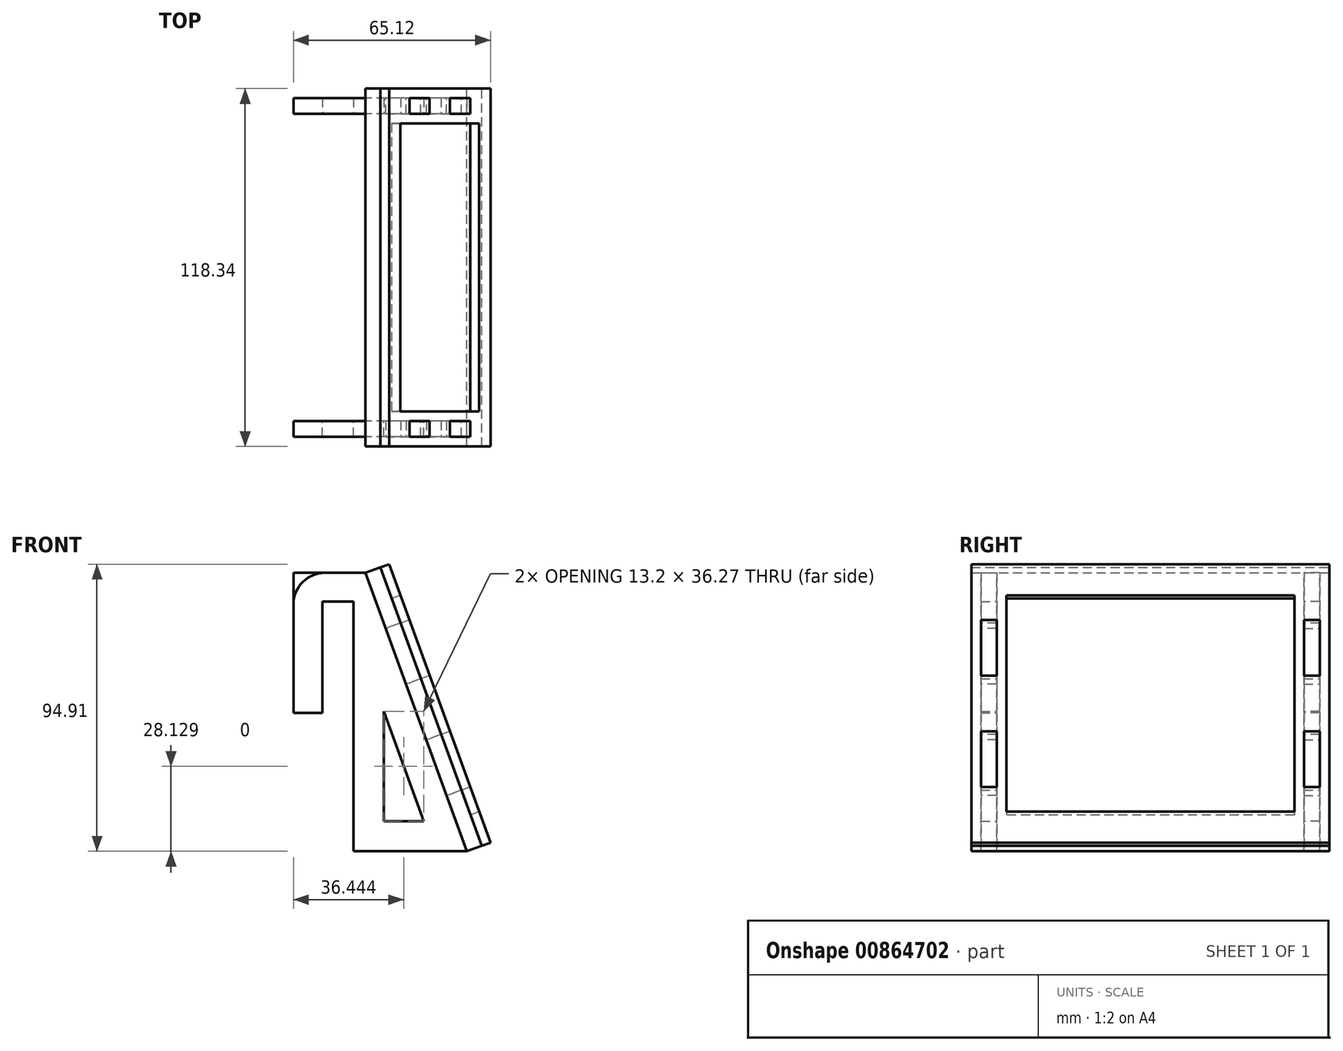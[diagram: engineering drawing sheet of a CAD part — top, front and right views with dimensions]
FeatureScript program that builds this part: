
annotation { "Feature Type Name" : "Feature", "Feature Type Description" : "" }
export const myFeature = defineFeature(function(context is Context, id is Id, definition is map)
    precondition{}
    {
        {
            assignVariable(context, id + "F0", {"name" : "thickness", "anyValue" : 5.2});
        }
        {
            var Q0;
            Q0=qCreatedBy(makeId("Front.planeOp"),FACE);
            cPlane(context, id + "F1", {"entities" : qUnion([Q0]), "cplaneType" : CPlaneType.OFFSET, "offset" : 50.8 * mm, "width" : 150 * mm, "height" : 150 * mm});
        }
        {
            var Q0;
            Q0=qCreatedBy(id+"F1.planeOp",FACE);
            var sketch = newSketch(context, id + "F2", { "sketchPlane" : qUnion([Q0])});
            skLineSegment(sketch, "E0", {"start": v(9.52, 0) * mm, "end": v(9.52, 36.73) * mm});
            skLineSegment(sketch, "E1", {"start": v(9.52, 36.73) * mm, "end": v(19.84, 36.73) * mm});
            skLineSegment(sketch, "E2", {"start": v(19.84, 36.73) * mm, "end": v(19.84, -45.82) * mm});
            skLineSegment(sketch, "E3", {"start": v(19.84, -45.82) * mm, "end": v(57.33, -45.82) * mm});
            skLineSegment(sketch, "E4", {"start": v(57.33, -45.82) * mm, "end": v(23.81, 46.25) * mm});
            skLineSegment(sketch, "E5", {"start": v(23.81, 46.25) * mm, "end": v(0, 46.25) * mm});
            skLineSegment(sketch, "E6", {"start": v(0, 46.25) * mm, "end": v(0, 0) * mm});
            skLineSegment(sketch, "E7", {"start": v(0, 0) * mm, "end": v(9.52, 0) * mm});
            skLineSegment(sketch, "E8", {"start": v(14.68, 36.73) * mm, "end": v(14.68, 46.25) * mm, "construction": true});
            skLineSegment(sketch, "E9", {"start": v(19.84, 36.73) * mm, "end": v(19.84, 46.25) * mm, "construction": true});
            skLineSegment(sketch, "E10.0", {"start": v(43.04, -35.82) * mm, "end": v(29.84, 0.44) * mm});
            skLineSegment(sketch, "E10.1", {"start": v(29.84, -35.82) * mm, "end": v(43.04, -35.82) * mm});
            skLineSegment(sketch, "E10.2", {"start": v(29.84, 0.44) * mm, "end": v(29.84, -35.82) * mm});
            skSolve(sketch);
        }
        {
            var Q0;
            Q0=makeQuery(id+"F2.imprint","IMPRINT",FACE,{"disambiguationData":[TD([[makeQuery(id+"F2.imprint","IMPRINT",EDGE,{"derivedFrom":sQuery(id+"F2.wireOp",EDGE,"E0")}),1.0]])]});
            extrude(context, id + "F3", {"entities" : qUnion([Q0]), "depth" : (getVariable(context, 'thickness')) * mm, "offsetDistance" : 25 * mm});
        }
        {
            var Q0;
            Q0=makeQuery(id+"F3.opExtrude","SWEPT_FACE",FACE,{"disambiguationData":[OSD([sQuery(id+"F2.wireOp",EDGE,"E4")])]});
            var sketch = newSketch(context, id + "F4", { "sketchPlane" : qUnion([Q0])});
            skLineSegment(sketch, "E11.0.0", {"start": v(-50.8, -62.67) * mm, "end": v(-50.8, 35.32) * mm});
            skLineSegment(sketch, "E11.0.1", {"start": v(-50.8, 35.32) * mm, "end": v(-56, 35.32) * mm});
            skLineSegment(sketch, "E11.0.2", {"start": v(-56, 35.32) * mm, "end": v(-56, -62.67) * mm});
            skLineSegment(sketch, "E11.0.3", {"start": v(-56, -62.67) * mm, "end": v(-50.8, -62.67) * mm});
            skLineSegment(sketch, "E12.bottom", {"start": v(-50.8, 15.72) * mm, "end": v(-56, 15.72) * mm});
            skLineSegment(sketch, "E12.top", {"start": v(-50.8, -3.88) * mm, "end": v(-56, -3.88) * mm});
            skLineSegment(sketch, "E12.left", {"start": v(-50.8, 15.72) * mm, "end": v(-50.8, -3.88) * mm});
            skLineSegment(sketch, "E12.right", {"start": v(-56, 15.72) * mm, "end": v(-56, -3.88) * mm});
            skLineSegment(sketch, "E13.bottom", {"start": v(-50.8, -23.47) * mm, "end": v(-56, -23.47) * mm});
            skLineSegment(sketch, "E13.top", {"start": v(-50.8, -43.07) * mm, "end": v(-56, -43.07) * mm});
            skLineSegment(sketch, "E13.left", {"start": v(-50.8, -23.47) * mm, "end": v(-50.8, -43.07) * mm});
            skLineSegment(sketch, "E13.right", {"start": v(-56, -23.47) * mm, "end": v(-56, -43.07) * mm});
            skLineSegment(sketch, "E14", {"start": v(-53.4, 35.32) * mm, "end": v(-53.4, 15.72) * mm, "construction": true});
            skLineSegment(sketch, "E15", {"start": v(-53.4, -43.07) * mm, "end": v(-53.4, -62.67) * mm, "construction": true});
            skLineSegment(sketch, "E16", {"start": v(-53.4, 15.72) * mm, "end": v(-53.4, -3.88) * mm, "construction": true});
            skLineSegment(sketch, "E17", {"start": v(-53.4, -3.88) * mm, "end": v(-53.4, -23.47) * mm, "construction": true});
            skLineSegment(sketch, "E18", {"start": v(-53.4, -23.47) * mm, "end": v(-53.4, -43.07) * mm, "construction": true});
            skSolve(sketch);
        }
        {
            var Q0;
            Q0=makeQuery(id+"F4.imprint","IMPRINT",FACE,{"disambiguationData":[TD([[makeQuery(id+"F4.imprint","IMPRINT",EDGE,{"derivedFrom":sQuery(id+"F4.wireOp",EDGE,"E12.bottom")}),1.0]])]});
            var Q1;
            Q1=makeQuery(id+"F4.imprint","IMPRINT",FACE,{"disambiguationData":[TD([[makeQuery(id+"F4.imprint","IMPRINT",EDGE,{"derivedFrom":sQuery(id+"F4.wireOp",EDGE,"E13.bottom")}),1.0]])]});
            extrude(context, id + "F5", {"entities" : qUnion([Q0, Q1]), "operationType" : NewBodyOperationType.ADD, "depth" : (getVariable(context, 'thickness') + 3.1) * mm, "offsetDistance" : 25 * mm});
        }
        {
            var Q0;
            Q0=makeQuery(id+"F3.opExtrude","SWEPT_BODY",BODY,{"disambiguationData":[OSD([sQuery(id+"F2.wireOp",EDGE,"E0"),sQuery(id+"F2.wireOp",EDGE,"E1"),sQuery(id+"F2.wireOp",EDGE,"E2"),sQuery(id+"F2.wireOp",EDGE,"E3"),sQuery(id+"F2.wireOp",EDGE,"E4"),sQuery(id+"F2.wireOp",EDGE,"E5"),sQuery(id+"F2.wireOp",EDGE,"E6"),sQuery(id+"F2.wireOp",EDGE,"E7"),sQuery(id+"F2.wireOp",EDGE,"013d1d72-8f7b-4af2-89c1-0a6e57d8ea99.0"),sQuery(id+"F2.wireOp",EDGE,"013d1d72-8f7b-4af2-89c1-0a6e57d8ea99.1"),sQuery(id+"F2.wireOp",EDGE,"013d1d72-8f7b-4af2-89c1-0a6e57d8ea99.2")])]});
            var Q1;
            Q1=qCreatedBy(makeId("Front.planeOp"),FACE);
            mirror(context, id + "F6", {"entities" : qUnion([Q0]), "mirrorPlane" : qUnion([Q1])});
        }
        {
            var Q0;
            {var subQ5=sQuery(id+"F2.wireOp",EDGE,"E5");var subQ6=sQuery(id+"F2.wireOp",EDGE,"E4");Q0=makeQuery(id+"F5.boolean.opBoolean","SPLIT",FACE,{"disambiguationData":[TD([makeQuery(id+"F3.opExtrude","SWEPT_FACE",FACE,{"disambiguationData":[OSD([subQ5])]})])],"derivedFrom":makeQuery(id+"F3.opExtrude","SWEPT_FACE",FACE,{"disambiguationData":[OSD([subQ6])]})});}
            var sketch = newSketch(context, id + "F7", { "sketchPlane" : qUnion([Q0])});
            skLineSegment(sketch, "E19.bottom", {"start": v(-59.18, 35.32) * mm, "end": v(59.18, 35.32) * mm});
            skLineSegment(sketch, "E19.top", {"start": v(-59.18, -62.67) * mm, "end": v(59.18, -62.67) * mm});
            skLineSegment(sketch, "E19.left", {"start": v(-59.18, 35.32) * mm, "end": v(-59.18, -62.67) * mm});
            skLineSegment(sketch, "E19.right", {"start": v(59.18, 35.32) * mm, "end": v(59.18, -62.67) * mm});
            skPoint(sketch, "E20.0", {"position": v(-56, 25.52) * mm});
            skLineSegment(sketch, "E21.0.0", {"start": v(-56, 15.72) * mm, "end": v(-50.8, 15.72) * mm, "construction": true});
            skLineSegment(sketch, "E21.0.1", {"start": v(-50.8, 15.72) * mm, "end": v(-50.8, 35.32) * mm, "construction": true});
            skLineSegment(sketch, "E21.0.2", {"start": v(-50.8, 35.32) * mm, "end": v(-56, 35.32) * mm, "construction": true});
            skLineSegment(sketch, "E21.0.3", {"start": v(-56, 35.32) * mm, "end": v(-56, 15.72) * mm, "construction": true});
            skLineSegment(sketch, "E22.0.0", {"start": v(50.8, -43.07) * mm, "end": v(50.8, -62.67) * mm, "construction": true});
            skLineSegment(sketch, "E22.0.1", {"start": v(50.8, -62.67) * mm, "end": v(56, -62.67) * mm, "construction": true});
            skLineSegment(sketch, "E22.0.2", {"start": v(56, -62.67) * mm, "end": v(56, -43.07) * mm, "construction": true});
            skLineSegment(sketch, "E22.0.3", {"start": v(56, -43.07) * mm, "end": v(50.8, -43.07) * mm, "construction": true});
            skLineSegment(sketch, "E23.0.0", {"start": v(-56, -3.88) * mm, "end": v(-50.8, -3.88) * mm});
            skLineSegment(sketch, "E23.0.1", {"start": v(-50.8, -3.88) * mm, "end": v(-50.8, 15.72) * mm});
            skLineSegment(sketch, "E23.0.2", {"start": v(-50.8, 15.72) * mm, "end": v(-56, 15.72) * mm});
            skLineSegment(sketch, "E23.0.3", {"start": v(-56, 15.72) * mm, "end": v(-56, -3.88) * mm});
            skLineSegment(sketch, "E24.0.0", {"start": v(-56, -43.07) * mm, "end": v(-50.8, -43.07) * mm});
            skLineSegment(sketch, "E24.0.1", {"start": v(-50.8, -43.07) * mm, "end": v(-50.8, -23.47) * mm});
            skLineSegment(sketch, "E24.0.2", {"start": v(-50.8, -23.47) * mm, "end": v(-56, -23.47) * mm});
            skLineSegment(sketch, "E24.0.3", {"start": v(-56, -23.47) * mm, "end": v(-56, -43.07) * mm});
            skLineSegment(sketch, "E25.0.0", {"start": v(50.8, -3.88) * mm, "end": v(56, -3.88) * mm});
            skLineSegment(sketch, "E25.0.1", {"start": v(56, -3.88) * mm, "end": v(56, 15.72) * mm});
            skLineSegment(sketch, "E25.0.2", {"start": v(56, 15.72) * mm, "end": v(50.8, 15.72) * mm});
            skLineSegment(sketch, "E25.0.3", {"start": v(50.8, 15.72) * mm, "end": v(50.8, -3.88) * mm});
            skLineSegment(sketch, "E26.0.0", {"start": v(50.8, -43.07) * mm, "end": v(56, -43.07) * mm});
            skLineSegment(sketch, "E26.0.1", {"start": v(56, -43.07) * mm, "end": v(56, -23.47) * mm});
            skLineSegment(sketch, "E26.0.2", {"start": v(56, -23.47) * mm, "end": v(50.8, -23.47) * mm});
            skLineSegment(sketch, "E26.0.3", {"start": v(50.8, -23.47) * mm, "end": v(50.8, -43.07) * mm});
            skLineSegment(sketch, "E27.bottom", {"start": v(47.62, 24.43) * mm, "end": v(-47.62, 24.43) * mm, "construction": true});
            skLineSegment(sketch, "E27.top", {"start": v(47.63, -51.77) * mm, "end": v(-47.62, -51.77) * mm, "construction": true});
            skLineSegment(sketch, "E27.left", {"start": v(47.63, 24.43) * mm, "end": v(47.63, -51.77) * mm, "construction": true});
            skLineSegment(sketch, "E27.right", {"start": v(-47.62, 24.43) * mm, "end": v(-47.62, -51.77) * mm, "construction": true});
            skLineSegment(sketch, "E28", {"start": v(-24.6, 24.43) * mm, "end": v(-24.6, 35.32) * mm, "construction": true});
            skLineSegment(sketch, "E29", {"start": v(-22.62, -51.77) * mm, "end": v(-22.62, -62.67) * mm, "construction": true});
            skLineSegment(sketch, "E30", {"start": v(-59.18, -9.77) * mm, "end": v(-47.62, -9.77) * mm, "construction": true});
            skLineSegment(sketch, "E31", {"start": v(59.18, -13.67) * mm, "end": v(47.63, -13.67) * mm, "construction": true});
            skLineSegment(sketch, "E32", {"start": v(-50.8, 9.46) * mm, "end": v(-47.62, 9.46) * mm, "construction": true});
            skLineSegment(sketch, "E33", {"start": v(50.8, 10.22) * mm, "end": v(47.62, 10.22) * mm, "construction": true});
            skLineSegment(sketch, "E34", {"start": v(56, 10.5) * mm, "end": v(59.18, 10.5) * mm, "construction": true});
            skLineSegment(sketch, "E35", {"start": v(-56, 12.25) * mm, "end": v(-59.18, 12.25) * mm, "construction": true});
            skSolve(sketch);
        }
        {
            var Q0;
            Q0=qSketchRegion(id+"F7",true);
            extrude(context, id + "F8", {"entities" : qUnion([Q0]), "depth" : (getVariable(context, 'thickness')) * mm, "offsetDistance" : 25 * mm});
        }
        {
            var Q0;
            Q0=makeQuery(id+"F8.opExtrude","CAP_FACE",FACE,{"disambiguationData":[OSD([sQuery(id+"F7.wireOp",EDGE,"E19.bottom"),sQuery(id+"F7.wireOp",EDGE,"E19.top"),sQuery(id+"F7.wireOp",EDGE,"E19.left"),sQuery(id+"F7.wireOp",EDGE,"E19.right"),sQuery(id+"F7.wireOp",EDGE,"E23.0.0"),sQuery(id+"F7.wireOp",EDGE,"E23.0.1"),sQuery(id+"F7.wireOp",EDGE,"E23.0.2"),sQuery(id+"F7.wireOp",EDGE,"E23.0.3"),sQuery(id+"F7.wireOp",EDGE,"E24.0.0"),sQuery(id+"F7.wireOp",EDGE,"E24.0.1"),sQuery(id+"F7.wireOp",EDGE,"E24.0.2"),sQuery(id+"F7.wireOp",EDGE,"E24.0.3"),sQuery(id+"F7.wireOp",EDGE,"E25.0.0"),sQuery(id+"F7.wireOp",EDGE,"E25.0.1"),sQuery(id+"F7.wireOp",EDGE,"E25.0.2"),sQuery(id+"F7.wireOp",EDGE,"E25.0.3"),sQuery(id+"F7.wireOp",EDGE,"E26.0.0"),sQuery(id+"F7.wireOp",EDGE,"E26.0.1"),sQuery(id+"F7.wireOp",EDGE,"E26.0.2"),sQuery(id+"F7.wireOp",EDGE,"E26.0.3")])],"isStart":false});
            var sketch = newSketch(context, id + "F9", { "sketchPlane" : qUnion([Q0])});
            skLineSegment(sketch, "E36.0", {"start": v(-59.18, -62.67) * mm, "end": v(59.18, -62.67) * mm});
            skLineSegment(sketch, "E37.0", {"start": v(-59.18, 35.32) * mm, "end": v(59.18, 35.32) * mm});
            skLineSegment(sketch, "E38.0", {"start": v(59.18, 35.32) * mm, "end": v(59.18, -62.67) * mm});
            skLineSegment(sketch, "E39.0", {"start": v(-59.18, 35.32) * mm, "end": v(-59.18, -62.67) * mm});
            skLineSegment(sketch, "E40.0.0", {"start": v(-56, -3.88) * mm, "end": v(-50.8, -3.88) * mm});
            skLineSegment(sketch, "E40.0.1", {"start": v(-50.8, -3.88) * mm, "end": v(-50.8, 15.72) * mm});
            skLineSegment(sketch, "E40.0.2", {"start": v(-50.8, 15.72) * mm, "end": v(-56, 15.72) * mm});
            skLineSegment(sketch, "E40.0.3", {"start": v(-56, 15.72) * mm, "end": v(-56, -3.88) * mm});
            skLineSegment(sketch, "E41.0.0", {"start": v(50.8, -3.88) * mm, "end": v(56, -3.88) * mm});
            skLineSegment(sketch, "E41.0.1", {"start": v(56, -3.88) * mm, "end": v(56, 15.72) * mm});
            skLineSegment(sketch, "E41.0.2", {"start": v(56, 15.72) * mm, "end": v(50.8, 15.72) * mm});
            skLineSegment(sketch, "E41.0.3", {"start": v(50.8, 15.72) * mm, "end": v(50.8, -3.88) * mm});
            skLineSegment(sketch, "E42.0.0", {"start": v(50.8, -43.07) * mm, "end": v(56, -43.07) * mm});
            skLineSegment(sketch, "E42.0.1", {"start": v(56, -43.07) * mm, "end": v(56, -23.47) * mm});
            skLineSegment(sketch, "E42.0.2", {"start": v(56, -23.47) * mm, "end": v(50.8, -23.47) * mm});
            skLineSegment(sketch, "E42.0.3", {"start": v(50.8, -23.47) * mm, "end": v(50.8, -43.07) * mm});
            skLineSegment(sketch, "E43.0.0", {"start": v(-56, -43.07) * mm, "end": v(-50.8, -43.07) * mm});
            skLineSegment(sketch, "E43.0.1", {"start": v(-50.8, -43.07) * mm, "end": v(-50.8, -23.47) * mm});
            skLineSegment(sketch, "E43.0.2", {"start": v(-50.8, -23.47) * mm, "end": v(-56, -23.47) * mm});
            skLineSegment(sketch, "E43.0.3", {"start": v(-56, -23.47) * mm, "end": v(-56, -43.07) * mm});
            skLineSegment(sketch, "E44.0", {"start": v(47.62, 24.43) * mm, "end": v(-47.62, 24.43) * mm});
            skLineSegment(sketch, "E45.0", {"start": v(-47.62, 24.43) * mm, "end": v(-47.62, -51.77) * mm});
            skLineSegment(sketch, "E46.0", {"start": v(47.63, -51.77) * mm, "end": v(-47.62, -51.77) * mm});
            skLineSegment(sketch, "E47.0", {"start": v(47.63, 24.43) * mm, "end": v(47.63, -51.77) * mm});
            skSolve(sketch);
        }
        {
            var Q0;
            Q0 = qSketchRegion(id + "F9", true);
            extrude(context, id + "F10", {"entities" : qUnion([Q0]), "depth" : 3.1 * mm, "offsetDistance" : 25 * mm});
        }
        {
            var Q0;
            Q0=makeQuery(id+"F3.opExtrude","SWEPT_EDGE",EDGE,{"disambiguationData":[OSD([sQuery(id+"F2.wireOp",EDGE,"E5"),sQuery(id+"F2.wireOp",EDGE,"E6")])]});
            fillet(context, id + "F11", {"entities" : qUnion([Q0]), "radius" : 10.38 * mm, "tangentPropagation" : true, "allowEdgeOverflow" : false});
        }
    });
